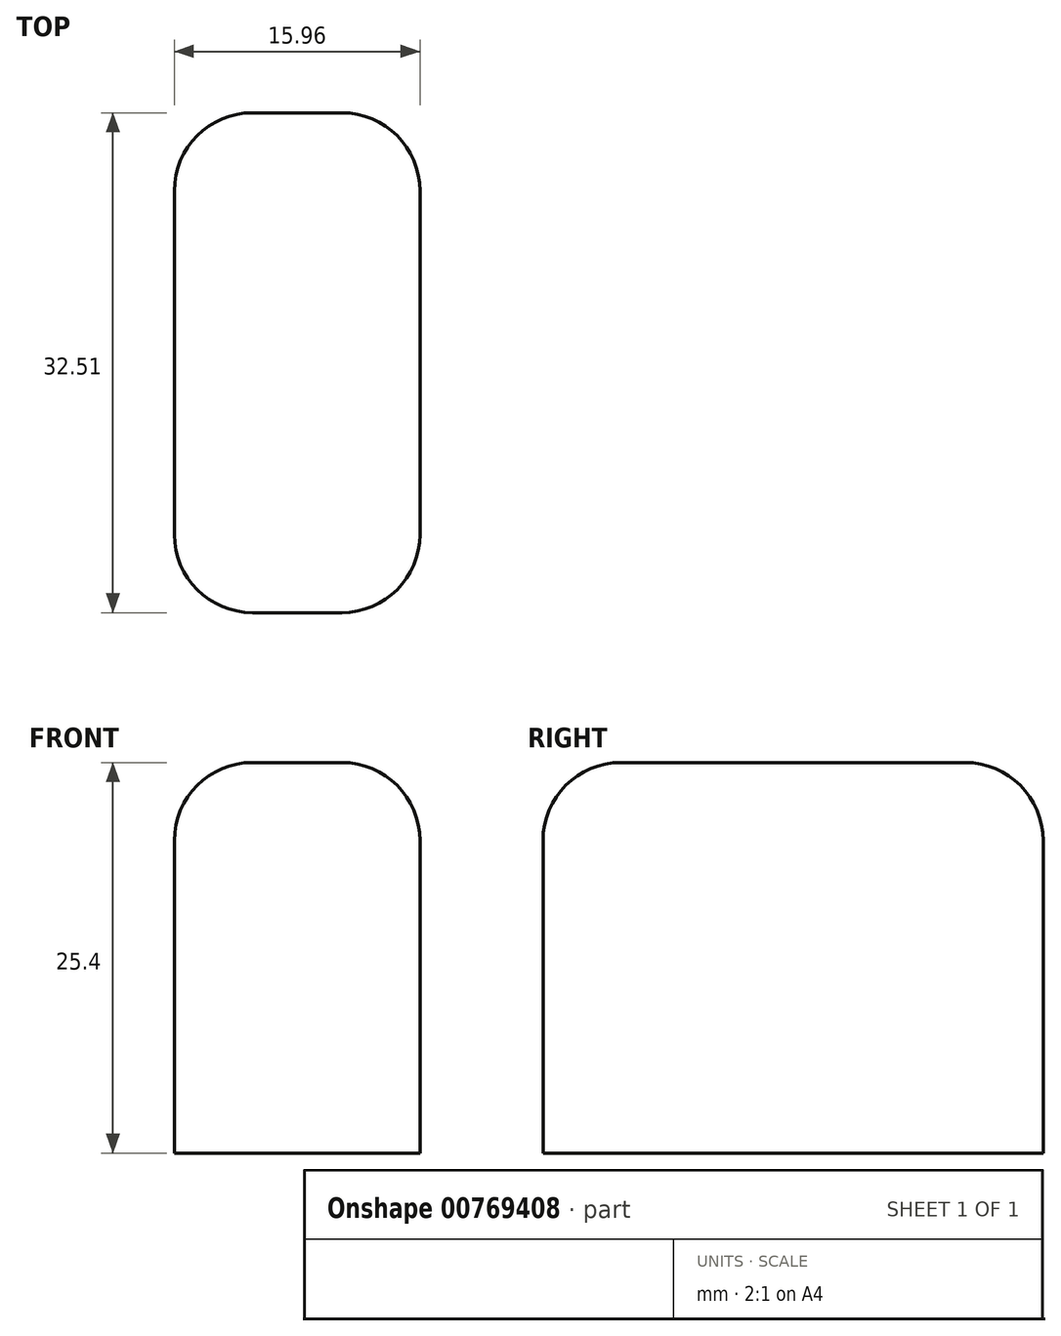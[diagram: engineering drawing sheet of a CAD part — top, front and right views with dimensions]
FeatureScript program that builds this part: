
annotation { "Feature Type Name" : "Feature", "Feature Type Description" : "" }
export const myFeature = defineFeature(function(context is Context, id is Id, definition is map)
    precondition{}
    {
        {
            var Q0;
            Q0=qCreatedBy(makeId("Top.planeOp"),FACE);
            var sketch = newSketch(context, id + "F0", { "sketchPlane" : qUnion([Q0])});
            skLineSegment(sketch, "E0.bottom", {"start": v(-17.8, -17.46) * mm, "end": v(-33.76, -17.46) * mm});
            skLineSegment(sketch, "E0.top", {"start": v(-17.8, 15.05) * mm, "end": v(-33.76, 15.05) * mm});
            skLineSegment(sketch, "E0.left", {"start": v(-17.8, -17.46) * mm, "end": v(-17.8, 15.05) * mm});
            skLineSegment(sketch, "E0.right", {"start": v(-33.76, -17.46) * mm, "end": v(-33.76, 15.05) * mm});
            skPoint(sketch, "E0.middle", {"position": v(-25.78, -1.2) * mm});
            skSolve(sketch);
        }
        {
            var Q0;
            Q0=makeQuery(id+"F0.imprint","IMPRINT",FACE,{"disambiguationData":[TD([[makeQuery(id+"F0.imprint","IMPRINT",EDGE,{"derivedFrom":sQuery(id+"F0.wireOp",EDGE,"E0.bottom")}),-1.0]])]});
            extrude(context, id + "F1", {"entities" : qUnion([Q0]), "depth" : 25.4 * mm, "offsetDistance" : 25.4 * mm});
        }
        {
            var Q0;
            Q0=makeQuery(id+"F1.opExtrude","CAP_EDGE",EDGE,{"disambiguationData":[OSD([sQuery(id+"F0.wireOp",EDGE,"E0.bottom")])],"isStart":false});
            var Q1;
            Q1=makeQuery(id+"F1.opExtrude","CAP_EDGE",EDGE,{"disambiguationData":[OSD([sQuery(id+"F0.wireOp",EDGE,"E0.left")])],"isStart":false});
            var Q2;
            Q2=makeQuery(id+"F1.opExtrude","CAP_EDGE",EDGE,{"disambiguationData":[OSD([sQuery(id+"F0.wireOp",EDGE,"E0.right")])],"isStart":false});
            var Q3;
            Q3=makeQuery(id+"F1.opExtrude","SWEPT_EDGE",EDGE,{"disambiguationData":[OSD([sQuery(id+"F0.wireOp",EDGE,"E0.bottom"),sQuery(id+"F0.wireOp",EDGE,"E0.left")])]});
            var Q4;
            Q4=makeQuery(id+"F1.opExtrude","SWEPT_EDGE",EDGE,{"disambiguationData":[OSD([sQuery(id+"F0.wireOp",EDGE,"E0.bottom"),sQuery(id+"F0.wireOp",EDGE,"E0.right")])]});
            var Q5;
            Q5=makeQuery(id+"F1.opExtrude","SWEPT_EDGE",EDGE,{"disambiguationData":[OSD([sQuery(id+"F0.wireOp",EDGE,"E0.top"),sQuery(id+"F0.wireOp",EDGE,"E0.left")])]});
            var Q6;
            Q6=makeQuery(id+"F1.opExtrude","SWEPT_EDGE",EDGE,{"disambiguationData":[OSD([sQuery(id+"F0.wireOp",EDGE,"E0.top"),sQuery(id+"F0.wireOp",EDGE,"E0.right")])]});
            var Q7;
            Q7=makeQuery(id+"F1.opExtrude","CAP_EDGE",EDGE,{"disambiguationData":[OSD([sQuery(id+"F0.wireOp",EDGE,"E0.top")])],"isStart":false});
            fillet(context, id + "F2", {"entities" : qUnion([Q0, Q1, Q2, Q3, Q4, Q5, Q6, Q7]), "radius" : 5.08 * mm, "tangentPropagation" : true, "allowEdgeOverflow" : false});
        }
    });
